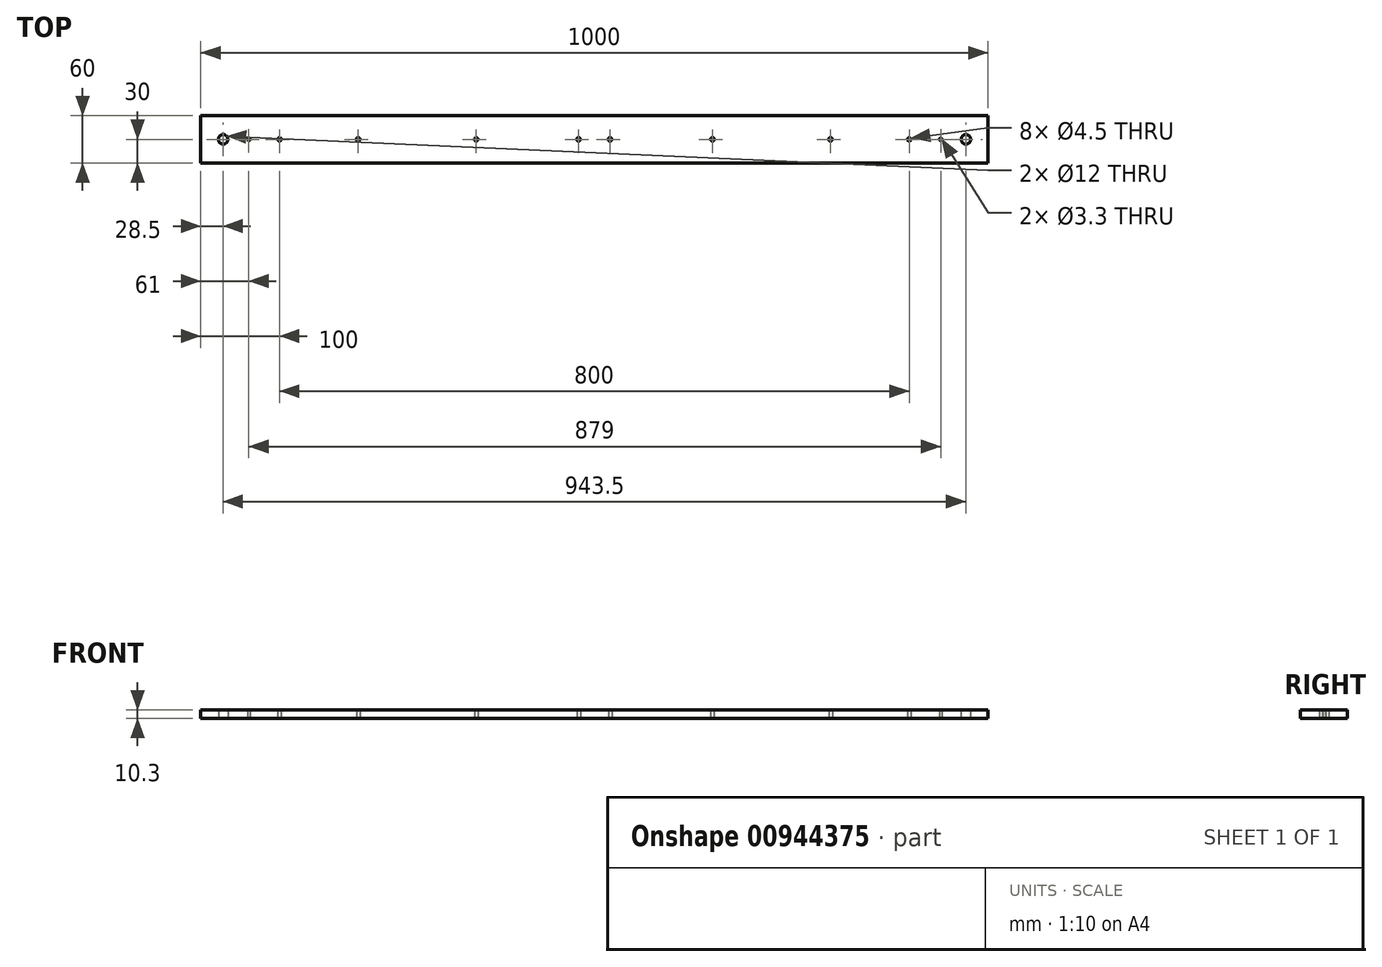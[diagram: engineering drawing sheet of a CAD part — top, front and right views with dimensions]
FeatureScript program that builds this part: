
annotation { "Feature Type Name" : "Feature", "Feature Type Description" : "" }
export const myFeature = defineFeature(function(context is Context, id is Id, definition is map)
    precondition{}
    {
        {
            var Q0;
            Q0=qCreatedBy(makeId("Top.planeOp"),FACE);
            var sketch = newSketch(context, id + "F0", { "sketchPlane" : qUnion([Q0])});
            skLineSegment(sketch, "E0.bottom", {"start": v(-500, 30) * mm, "end": v(500, 30) * mm});
            skLineSegment(sketch, "E0.top", {"start": v(-500, -30) * mm, "end": v(500, -30) * mm});
            skLineSegment(sketch, "E0.left", {"start": v(-500, 30) * mm, "end": v(-500, -30) * mm});
            skLineSegment(sketch, "E0.right", {"start": v(500, 30) * mm, "end": v(500, -30) * mm});
            skPoint(sketch, "E0.middle", {"position": v(0, 0) * mm});
            skLineSegment(sketch, "E1", {"start": v(-519.29, 0) * mm, "end": v(537.98, 0) * mm, "construction": true});
            skCircle(sketch, "E2", {"center": v(-471.5, 0) * mm, "radius": 6 * mm});
            skCircle(sketch, "E3", {"center": v(-439, 0) * mm, "radius": 1.65 * mm});
            skCircle(sketch, "E4", {"center": v(-400, 0) * mm, "radius": 2.25 * mm});
            skCircle(sketch, "E5", {"center": v(-300, 0) * mm, "radius": 2.25 * mm});
            skCircle(sketch, "E6", {"center": v(-150, 0) * mm, "radius": 2.25 * mm});
            skCircle(sketch, "E7", {"center": v(-20, 0) * mm, "radius": 2.25 * mm});
            skCircle(sketch, "E8", {"center": v(20, 0) * mm, "radius": 2.25 * mm});
            skLineSegment(sketch, "E9", {"start": v(0, 46.94) * mm, "end": v(0, -48.59) * mm, "construction": true});
            skPoint(sketch, "E9.startSnap0", {"position": v(0, 30) * mm});
            skPoint(sketch, "E9.endSnap0", {"position": v(0, -30) * mm});
            skCircle(sketch, "E10", {"center": v(150, 0) * mm, "radius": 2.25 * mm});
            skCircle(sketch, "E11", {"center": v(300, 0) * mm, "radius": 2.25 * mm});
            skCircle(sketch, "E12", {"center": v(400, 0) * mm, "radius": 2.25 * mm});
            skCircle(sketch, "E13", {"center": v(440, 0) * mm, "radius": 1.65 * mm});
            skCircle(sketch, "E14", {"center": v(472, 0) * mm, "radius": 6 * mm});
            skSolve(sketch);
        }
        {
            var Q0;
            Q0=makeQuery(id+"F0.imprint","IMPRINT",FACE,{"disambiguationData":[TD([[makeQuery(id+"F0.imprint","IMPRINT",EDGE,{"derivedFrom":sQuery(id+"F0.wireOp",EDGE,"E0.bottom")}),-1.0]])]});
            extrude(context, id + "F1", {"entities" : qUnion([Q0]), "depth" : 10.3 * mm, "offsetDistance" : 25 * mm});
        }
    });
